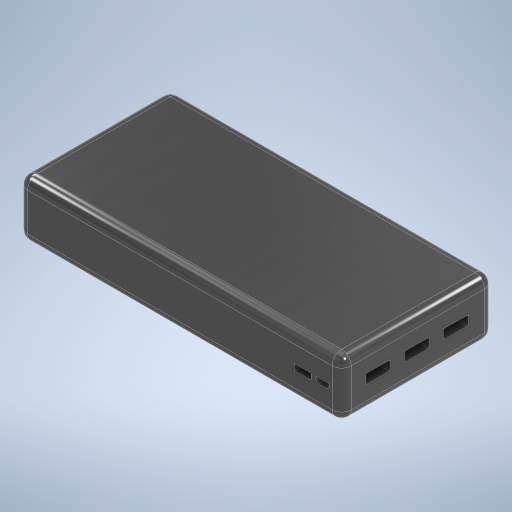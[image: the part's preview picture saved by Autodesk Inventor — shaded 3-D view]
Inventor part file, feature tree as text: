
AUTODESK INVENTOR PART (.ipt)
format: ipt  version: 2024 (Build 280153000, 153)  size: 359,424 bytes
history: native  units: in
note: dims shown in document units (in); Inventor stores cm internally (conversion verified against a paired STEP export)
features: extrude x4, sketch x4, fillet x1
ambient origin geometry x8: Origin, YZ Plane, XZ Plane, XY Plane, X Axis, Y Axis, Z Axis, Center Point
bodies: Solid1 (feature_tree)
feature tree (9):
  extrude  "Extrusion1"  Depth=3.1496in
  fillet  "Fillet1"  Radius=1.1811in
  extrude  "Extrusion2"  Depth=0.352in
  extrude  "Extrusion3"  Depth=0.1283in
  extrude  "Extrusion4"  TaperAngle=45.0deg  [1 undecoded]
  sketch  "Sketch1"  dims[d1=6.6929in d2=3.1496in d3=1.1811in d4=0.0in]
  sketch  "Sketch2"  dims[d5=0.1969in d6=0.352in]
  sketch  "Sketch3"  dims[d7=0.1283in d8=5.5118in]
  sketch  "Sketch4"  dims[d9=0.0197in d12=45.0deg d13=-0.0in d14=0.0492in d15=0.0197in d16=0.2717in d17=45.0deg d18=0.1181in d19=0.1969in d20=0.0in d21=0.5118in d22=0.1969in d23=0.5118in d24=0.1969in d25=0.5118in d26=0.1969in d27=0.2953in d28=0.2953in d32=0.5906in d33=0.0197in d34=0.1969in d35=0.0in d36=0.3937in d37=0.8858in d38=0.5906in d39=0.3543in d40=0.0984in d41=90.0deg d42=0.0197in d43=0.0197in d44=0.0in]
note: 1 required parameter value undecoded (feature->parameter linkage not recoverable at this tier; creation-order binding heuristic only, values carry confidence <= 0.55)
